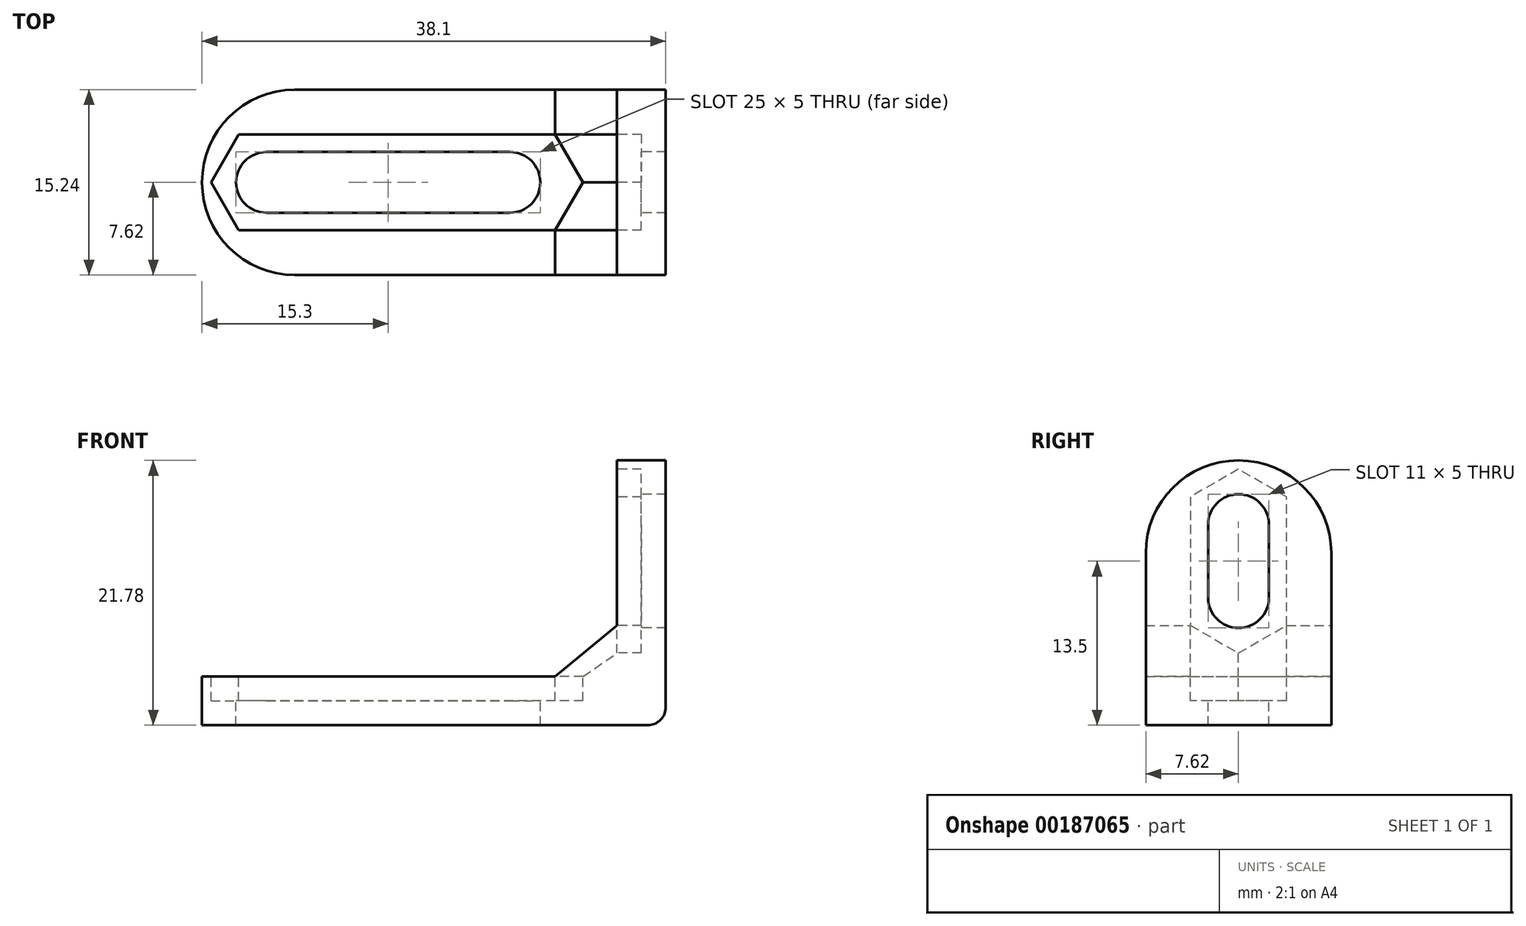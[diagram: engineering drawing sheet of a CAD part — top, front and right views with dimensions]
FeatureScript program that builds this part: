
annotation { "Feature Type Name" : "Feature", "Feature Type Description" : "" }
export const myFeature = defineFeature(function(context is Context, id is Id, definition is map)
    precondition{}
    {
        {
            var Q0;
            Q0=qCreatedBy(makeId("Front.planeOp"),FACE);
            var sketch = newSketch(context, id + "F0", { "sketchPlane" : qUnion([Q0])});
            skLineSegment(sketch, "E0.top", {"start": v(-4, 10.62) * mm, "end": v(-38.1, 10.62) * mm});
            skLineSegment(sketch, "E1.top", {"start": v(-1.5, 28.4) * mm, "end": v(-1.5, 28.4) * mm});
            skLineSegment(sketch, "E1.left", {"start": v(0, 8.12) * mm, "end": v(0, 28.4) * mm});
            skLineSegment(sketch, "E1.right", {"start": v(-4, 10.62) * mm, "end": v(-4, 28.4) * mm});
            skPoint(sketch, "E2.visualSharp", {"position": v(-4, 10.62) * mm});
            skPoint(sketch, "E3.visualSharp", {"position": v(0, 0) * mm});
            skPoint(sketch, "E4.visualSharp", {"position": v(-4, 28.4) * mm});
            skPoint(sketch, "E5.visualSharp", {"position": v(0, 28.4) * mm});
            skPoint(sketch, "E6.visualSharp", {"position": v(-53.3, 10.62) * mm});
            skLineSegment(sketch, "E7", {"start": v(-38.1, 6.62) * mm, "end": v(-1.5, 6.62) * mm});
            skPoint(sketch, "E8.visualSharp", {"position": v(-53.3, 6.62) * mm});
            skPoint(sketch, "E9.visualSharp", {"position": v(0, 6.62) * mm});
            skArc(sketch, "E9.filletArc", {"start": v(-1.5, 6.62) * mm, "mid": v(-0.44, 7.06) * mm, "end": v(0, 8.12) * mm});
            skLineSegment(sketch, "E10", {"start": v(-4, 28.4) * mm, "end": v(0, 28.4) * mm});
            skLineSegment(sketch, "E11.trimOffspring", {"start": v(-38.1, 10.62) * mm, "end": v(-38.1, 6.62) * mm});
            skSolve(sketch);
        }
        {
            var Q0;
            Q0=qSketchRegion(id+"F0",true);
            extrude(context, id + "F1", {"entities" : qUnion([Q0]), "depth" : 15.24 * mm});
        }
        {
            var Q0;
            Q0=makeQuery(id+"F1.opExtrude","SWEPT_FACE",FACE,{"disambiguationData":[OSD([sQuery(id+"F0.wireOp",EDGE,"E1.right")])]});
            var sketch = newSketch(context, id + "F2", { "sketchPlane" : qUnion([Q0])});
            skLineSegment(sketch, "E12", {"start": v(7.62, 23.12) * mm, "end": v(7.62, 17.12) * mm});
            skArc(sketch, "E13.0.startCap", {"start": v(5.12, 23.12) * mm, "mid": v(7.62, 25.62) * mm, "end": v(10.12, 23.12) * mm});
            skArc(sketch, "E13.0.endCap", {"start": v(10.12, 17.12) * mm, "mid": v(7.62, 14.62) * mm, "end": v(5.12, 17.12) * mm});
            skLineSegment(sketch, "E13.0.left", {"start": v(10.12, 23.12) * mm, "end": v(10.12, 17.12) * mm});
            skLineSegment(sketch, "E13.0.right", {"start": v(5.12, 23.12) * mm, "end": v(5.12, 17.12) * mm});
            skLineSegment(sketch, "E14.0.left", {"start": v(11.57, 23.12) * mm, "end": v(11.57, 17.12) * mm});
            skLineSegment(sketch, "E14.0.right", {"start": v(3.67, 23.12) * mm, "end": v(3.67, 17.12) * mm});
            skArc(sketch, "E15.cCircle", {"start": v(3.67, 23.12) * mm, "mid": v(7.62, 19.17) * mm, "end": v(11.57, 23.12) * mm, "construction": true});
            skLineSegment(sketch, "E15.0", {"start": v(11.57, 25.4) * mm, "end": v(11.57, 20.84) * mm});
            skLineSegment(sketch, "E15.3", {"start": v(3.67, 20.84) * mm, "end": v(3.67, 25.4) * mm});
            skLineSegment(sketch, "E15.4", {"start": v(3.67, 25.4) * mm, "end": v(7.62, 27.68) * mm});
            skLineSegment(sketch, "E15.5", {"start": v(7.62, 27.68) * mm, "end": v(11.57, 25.4) * mm});
            skPoint(sketch, "E15.0.midPoint", {"position": v(11.57, 23.12) * mm});
            skArc(sketch, "E16.cCircle", {"start": v(11.57, 17.12) * mm, "mid": v(7.62, 21.07) * mm, "end": v(3.67, 17.12) * mm, "construction": true});
            skLineSegment(sketch, "E16.0", {"start": v(11.57, 19.4) * mm, "end": v(11.57, 14.84) * mm});
            skLineSegment(sketch, "E16.1", {"start": v(11.57, 14.84) * mm, "end": v(7.62, 12.56) * mm});
            skLineSegment(sketch, "E16.2", {"start": v(7.62, 12.56) * mm, "end": v(3.67, 14.84) * mm});
            skLineSegment(sketch, "E16.3", {"start": v(3.67, 14.84) * mm, "end": v(3.67, 19.4) * mm});
            skPoint(sketch, "E16.0.midPoint", {"position": v(11.57, 17.12) * mm});
            skPoint(sketch, "E17.orphan", {"position": v(7.62, 21.68) * mm});
            skSolve(sketch);
        }
        {
            var Q0;
            Q0=qSketchRegion(id+"F2",true);
            extrude(context, id + "F3", {"entities" : qUnion([Q0]), "operationType" : NewBodyOperationType.REMOVE, "oppositeDirection" : true, "depth" : 2 * mm});
        }
        {
            var Q0;
            Q0=makeQuery(id+"F3.boolean.opBoolean","SPLIT",FACE,{"disambiguationData":[TD([makeQuery(id+"F3.opExtrude","SWEPT_FACE",FACE,{"disambiguationData":[OSD([sQuery(id+"F2.wireOp",EDGE,"E13.0.startCap")])]})])],"derivedFrom":makeQuery(id+"F1.opExtrude","SWEPT_FACE",FACE,{"disambiguationData":[OSD([sQuery(id+"F0.wireOp",EDGE,"E1.right")])]})});
            extrude(context, id + "F4", {"entities" : qUnion([Q0]), "operationType" : NewBodyOperationType.REMOVE, "endBound" : BoundingType.UP_TO_NEXT, "oppositeDirection" : true, "depth" : 25.4 * mm});
        }
        {
            var Q0;
            Q0=makeQuery(id+"F1.opExtrude","SWEPT_FACE",FACE,{"disambiguationData":[OSD([sQuery(id+"F0.wireOp",EDGE,"E0.top")])]});
            var sketch = newSketch(context, id + "F5", { "sketchPlane" : qUnion([Q0])});
            skLineSegment(sketch, "E18", {"start": v(-32.8, -7.62) * mm, "end": v(-12.8, -7.62) * mm});
            skPoint(sketch, "E18.startSnap0", {"position": v(-4, -7.62) * mm});
            skPoint(sketch, "E18.endSnap0", {"position": v(-6.8, -7.62) * mm});
            skArc(sketch, "E19.0.startCap", {"start": v(-32.8, -10.12) * mm, "mid": v(-35.3, -7.62) * mm, "end": v(-32.8, -5.12) * mm});
            skArc(sketch, "E19.0.endCap", {"start": v(-12.8, -5.12) * mm, "mid": v(-10.3, -7.62) * mm, "end": v(-12.8, -10.12) * mm});
            skLineSegment(sketch, "E19.0.left", {"start": v(-32.8, -5.12) * mm, "end": v(-12.8, -5.12) * mm});
            skLineSegment(sketch, "E19.0.right", {"start": v(-32.8, -10.12) * mm, "end": v(-12.8, -10.12) * mm});
            skArc(sketch, "E20.cCircle", {"start": v(-32.8, -11.57) * mm, "mid": v(-28.85, -7.62) * mm, "end": v(-32.8, -3.67) * mm, "construction": true});
            skLineSegment(sketch, "E20.0", {"start": v(-9.08, -11.57) * mm, "end": v(-35.08, -11.57) * mm});
            skLineSegment(sketch, "E20.1", {"start": v(-35.08, -11.57) * mm, "end": v(-37.36, -7.62) * mm});
            skLineSegment(sketch, "E20.2", {"start": v(-37.36, -7.62) * mm, "end": v(-35.08, -3.67) * mm});
            skLineSegment(sketch, "E20.3", {"start": v(-35.08, -3.67) * mm, "end": v(-9.08, -3.67) * mm});
            skPoint(sketch, "E20.0.midPoint", {"position": v(-32.8, -11.57) * mm});
            skLineSegment(sketch, "E21.4", {"start": v(-9.08, -3.67) * mm, "end": v(-6.8, -7.62) * mm});
            skLineSegment(sketch, "E21.5", {"start": v(-6.8, -7.62) * mm, "end": v(-9.08, -11.57) * mm});
            skPoint(sketch, "E22.orphan", {"position": v(-28.24, -7.62) * mm});
            skSolve(sketch);
        }
        {
            var Q0;
            Q0=qSketchRegion(id+"F5",true);
            extrude(context, id + "F6", {"entities" : qUnion([Q0]), "operationType" : NewBodyOperationType.REMOVE, "oppositeDirection" : true, "depth" : 2 * mm});
        }
        {
            var Q0;
            Q0=makeQuery(id+"F6.boolean.opBoolean","SPLIT",FACE,{"disambiguationData":[TD([makeQuery(id+"F6.opExtrude","SWEPT_FACE",FACE,{"disambiguationData":[OSD([sQuery(id+"F5.wireOp",EDGE,"E19.0.startCap")])]})])],"derivedFrom":makeQuery(id+"F1.opExtrude","SWEPT_FACE",FACE,{"disambiguationData":[OSD([sQuery(id+"F0.wireOp",EDGE,"E0.top")])]})});
            extrude(context, id + "F7", {"entities" : qUnion([Q0]), "operationType" : NewBodyOperationType.REMOVE, "endBound" : BoundingType.UP_TO_NEXT, "oppositeDirection" : true, "depth" : 25.4 * mm});
        }
        {
            var Q0;
            Q0=makeQuery(id+"F1.opExtrude","CAP_EDGE",EDGE,{"disambiguationData":[OSD([sQuery(id+"F0.wireOp",EDGE,"E11.trimOffspring")])],"isStart":false});
            var Q1;
            Q1=makeQuery(id+"F1.opExtrude","CAP_EDGE",EDGE,{"disambiguationData":[OSD([sQuery(id+"F0.wireOp",EDGE,"E11.trimOffspring")])],"isStart":true});
            fillet(context, id + "F8", {"entities" : qUnion([Q0, Q1]), "radius" : 7.62 * mm, "tangentPropagation" : true, "allowEdgeOverflow" : false});
        }
        {
            var Q0;
            {var subQ0=sQuery(id+"F0.wireOp",EDGE,"E1.right");var subQ6=sQuery(id+"F0.wireOp",EDGE,"E0.top");Q0=makeQuery(id+"F6.boolean.opBoolean","SPLIT",FACE,{"disambiguationData":[TD([makeQuery(id+"F1.opExtrude","SWEPT_FACE",FACE,{"disambiguationData":[OSD([subQ0])]})])],"derivedFrom":makeQuery(id+"F1.opExtrude","SWEPT_FACE",FACE,{"disambiguationData":[OSD([subQ6])]})});}
            var sketch = newSketch(context, id + "F9", { "sketchPlane" : qUnion([Q0])});
            skLineSegment(sketch, "E23.top", {"start": v(-9.08, -15.24) * mm, "end": v(-4, -15.24) * mm});
            skLineSegment(sketch, "E23.left", {"start": v(-9.08, 0) * mm, "end": v(-9.08, -15.24) * mm});
            skLineSegment(sketch, "E23.right", {"start": v(-4, 0) * mm, "end": v(-4, -15.24) * mm});
            skLineSegment(sketch, "E24.top", {"start": v(-9.08, 0) * mm, "end": v(-4, 0) * mm});
            skSolve(sketch);
        }
        {
            var Q0;
            {var subQ4=sQuery(id+"F0.wireOp",EDGE,"E1.right");var subQ6=sQuery(id+"F0.wireOp",EDGE,"E0.top");Q0=makeQuery(id+"F3.boolean.opBoolean","SPLIT",FACE,{"disambiguationData":[TD([makeQuery(id+"F1.opExtrude","SWEPT_FACE",FACE,{"disambiguationData":[OSD([subQ6])]})])],"derivedFrom":makeQuery(id+"F1.opExtrude","SWEPT_FACE",FACE,{"disambiguationData":[OSD([subQ4])]})});}
            var sketch = newSketch(context, id + "F10", { "sketchPlane" : qUnion([Q0])});
            skLineSegment(sketch, "E25.right", {"start": v(0, 14.84) * mm, "end": v(0, 10.62) * mm});
            skLineSegment(sketch, "E26.bottom", {"start": v(15.24, 10.62) * mm, "end": v(0, 10.62) * mm});
            skLineSegment(sketch, "E26.top", {"start": v(15.24, 14.84) * mm, "end": v(0, 14.84) * mm});
            skLineSegment(sketch, "E26.left", {"start": v(15.24, 10.62) * mm, "end": v(15.24, 14.84) * mm});
            skSolve(sketch);
        }
        {
            var Q0;
            {var subQ2=sQuery(id+"F9.wireOp",EDGE,"E23.top");Q0=makeQuery(id+"F9.imprint","IMPRINT",FACE,{"disambiguationData":[TD([[makeQuery(id+"F9.imprint","IMPRINT",EDGE,{"derivedFrom":subQ2}),-1.0]])]});}
            var Q1;
            {var subQ5=sQuery(id+"F10.wireOp",EDGE,"E25.right");Q1=makeQuery(id+"F10.imprint","IMPRINT",FACE,{"disambiguationData":[TD([[makeQuery(id+"F10.imprint","IMPRINT",EDGE,{"derivedFrom":subQ5}),-1.0]])]});}
            var Q2;
            Q2=makeQuery(id+"F9.imprint","IMPRINT",FACE,{"disambiguationData":[TD([[makeQuery(id+"F9.imprint","IMPRINT",EDGE,{"derivedFrom":sQuery(id+"F9.wireOp",EDGE,"bt2bfATN-E2v8-TheF-lZmc-CfuJhGe66lLX.bottom")}),1.0]])]});
            var Q3;
            Q3=makeQuery(id+"F10.imprint","IMPRINT",FACE,{"disambiguationData":[TD([[makeQuery(id+"F10.imprint","IMPRINT",EDGE,{"derivedFrom":sQuery(id+"F10.wireOp",EDGE,"E25.bottom")}),1.0]])]});
            var Q4;
            Q4=sQuery(id+"F9.wireOp",VERTEX,"E23.top.start");
            var Q5;
            Q5=sQuery(id+"F10.wireOp",VERTEX,"E26.left.end");
            loft(context, id + "F11", {"operationType" : NewBodyOperationType.ADD, "sheetProfilesArray" : [{ "sheetProfileEntities" : qUnion([Q0]) }, { "sheetProfileEntities" : qUnion([Q1]) }], "wireProfilesArray" : [{ "wireProfileEntities" : qUnion([Q2]) }, { "wireProfileEntities" : qUnion([Q3]) }], "matchConnections" : true, "connections" : [{ "connectionEntities" : qUnion([Q4, Q5]), "connectionEdgeQueries" : qUnion([]), "connectionEdgeParameters" : [] }]});
        }
        {
            var Q0;
            Q0=makeQuery(id+"F1.opExtrude","CAP_EDGE",EDGE,{"disambiguationData":[OSD([sQuery(id+"F0.wireOp",EDGE,"E10")])],"isStart":false});
            var Q1;
            Q1=makeQuery(id+"F1.opExtrude","CAP_EDGE",EDGE,{"disambiguationData":[OSD([sQuery(id+"F0.wireOp",EDGE,"E10")])],"isStart":true});
            fillet(context, id + "F12", {"entities" : qUnion([Q0, Q1]), "radius" : 7.62 * mm, "tangentPropagation" : true, "allowEdgeOverflow" : false});
        }
    });
